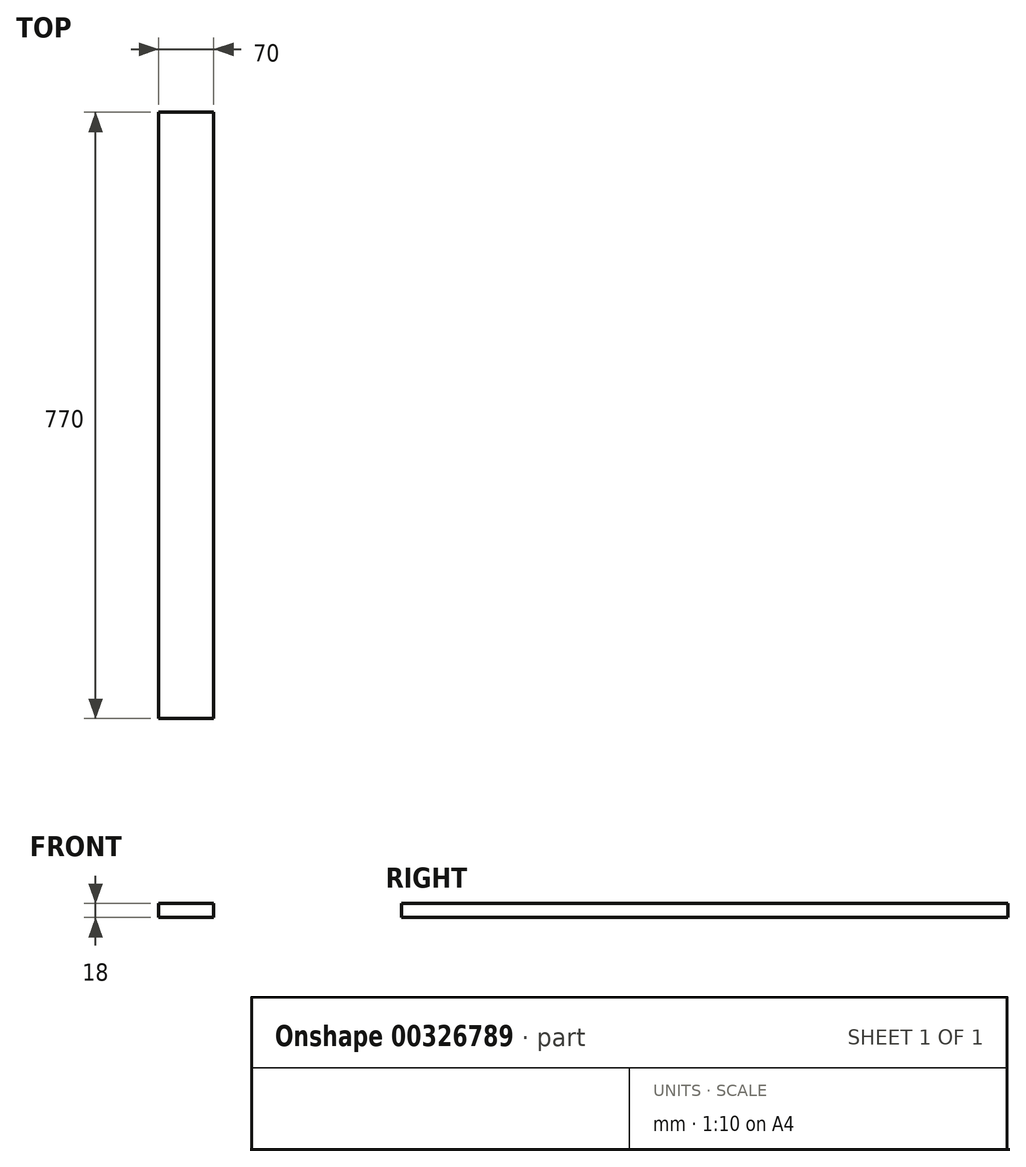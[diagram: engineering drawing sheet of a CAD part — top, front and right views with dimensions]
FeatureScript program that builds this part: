
annotation { "Feature Type Name" : "Feature", "Feature Type Description" : "" }
export const myFeature = defineFeature(function(context is Context, id is Id, definition is map)
    precondition{}
    {
        {
            var Q0;
            Q0=qCreatedBy(makeId("Top.planeOp"),FACE);
            var sketch = newSketch(context, id + "F0", { "sketchPlane" : qUnion([Q0])});
            skLineSegment(sketch, "E0.bottom", {"start": v(0, 0) * mm, "end": v(70, 0) * mm});
            skLineSegment(sketch, "E0.top", {"start": v(0, 770) * mm, "end": v(70, 770) * mm});
            skLineSegment(sketch, "E0.left", {"start": v(0, 0) * mm, "end": v(0, 770) * mm});
            skLineSegment(sketch, "E0.right", {"start": v(70, 0) * mm, "end": v(70, 770) * mm});
            skSolve(sketch);
        }
        {
            var Q0;
            Q0=qSketchRegion(id+"F0",true);
            extrude(context, id + "F1", {"entities" : qUnion([Q0]), "depth" : 18 * mm});
        }
    });
